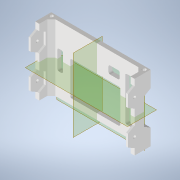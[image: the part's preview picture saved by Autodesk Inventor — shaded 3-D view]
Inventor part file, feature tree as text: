
AUTODESK INVENTOR PART (.ipt)
format: ipt  version: 2022.2 (Build 262287000, 287)  size: 368,128 bytes
history: native  units: mm
features: reference x24, extrude x12, sketch x12, projected_geometry x6, other x6, plane x3, chamfer x2, mirror x2, shell x1, fillet x1
ambient origin geometry x8: Origin, YZ Plane, XZ Plane, XY Plane, X Axis, Y Axis, Z Axis, Center Point
bodies: Solid1 (feature_tree)
feature tree (69):
  plane  "Work Plane1"
  extrude  "Extrusion1"  Depth=20.0mm
  extrude  "Extrusion2"  Depth=8.0mm TaperAngle=45.0deg
  chamfer  "Chamfer1"  Distance=25.0mm
  shell  "Shell1"  Thickness=150.0deg
  extrude  "Extrusion5"  Depth=20.0mm
  extrude  "Extrusion6"  TaperAngle=60.0deg  [1 undecoded]
  extrude  "Extrusion8"  Depth=8.0mm
  extrude  "Extrusion10"  Depth=8.0mm
  extrude  "Extrusion11"  Depth=8.0mm
  extrude  "Extrusion7"  Depth=10.0mm
  plane  "Work Plane3"
  plane  "Work Plane4"
  mirror  "Mirror2"
  mirror  "Mirror3"
  chamfer  "Chamfer4"  [1 undecoded]
  extrude  "Extrusion14"  TaperAngle=60.0deg  [1 undecoded]
  extrude  "Extrusion15"  TaperAngle=60.0deg  [1 undecoded]
  extrude  "Extrusion16"  Depth=8.0mm
  extrude  "Extrusion17"  Depth=62.5mm
  fillet  "Fillet6"  Radius=42.5mm
  sketch  "Sketch3"  dims[d1=20.0mm d2=0.0mm d3=4.0mm]
  reference  "Reference1"
  reference  "Reference2"
  reference  "Reference3"
  reference  "Reference4"
  reference  "Reference5"
  reference  "Reference6"
  reference  "Reference7"
  reference  "Reference8"
  reference  "Reference9"
  reference  "Reference10"
  reference  "Reference11"
  reference  "Reference12"
  sketch  "Sketch4"  dims[d4=0.0mm d5=0.0mm d6=8.0mm d7=2.0mm d8=45.0deg]
  reference  "Reference13"
  sketch  "Sketch7"  dims[d9=5.0mm d27=25.0mm d28=0.0mm d29=150.0deg]
  projected_geometry  "Projected Loop2"
  sketch  "Sketch8"  dims[d30=20.0mm d31=0.0mm d37=3.5mm]
  projected_geometry  "Projected Loop3"
  sketch  "Sketch10"  dims[d38=12.0mm d39=0.436332mm d43=60.0deg]
  projected_geometry  "Projected Loop5"
  sketch  "Sketch12"  dims[d44=60.0deg d45=8.0mm]
  projected_geometry  "Projected Loop7"
  sketch  "Sketch15"  dims[d46=15.0mm d47=8.0mm]
  projected_geometry  "Projected Loop9"
  sketch  "Sketch16"  dims[d48=2.5mm d49=0.0mm d53=8.0mm]
  projected_geometry  "Projected Loop10"
  sketch  "Sketch19"  dims[d59=10.0mm d60=0.0mm d61=3.5mm d62=0.0mm d63=0.0mm]
  reference  "Reference14"
  reference  "Reference15"
  reference  "Reference16"
  reference  "Reference17"
  sketch  "Sketch20"  dims[d67=0.5mm d68=2.0mm d69=45.0deg d79=60.0deg]
  reference  "Reference18"
  reference  "Reference19"
  reference  "Reference20"
  reference  "Reference21"
  sketch  "Sketch21"  dims[d80=60.0deg d81=60.0deg]
  reference  "Reference22"
  reference  "Reference23"
  sketch  "Sketch22"  dims[d82=60.0deg d84=8.0mm d85=62.5mm d86=42.5mm d87=0.0mm d88=0.0mm d90=8.0mm d91=8.0mm d92=12.0mm d93=12.0mm d94=2.0mm d95=0.0mm d96=0.0mm d98=2.0mm d99=0.0mm d100=0.0mm d102=2.0mm d103=0.0mm d104=0.0mm d105=2.0mm]
  reference  "Reference25"
  other  "<userpath>\Desktop\Jetson-Nano-2GB-Case\A.iam"
  other  "A.iam"
  other  "A-00:1"
  other  "Jetson Nano 2GB:1"
  other  "642-13541_BATUU_SYS_BOM_ASM:1"
  other  "600-13542-BASE-A02_ASM:1"
note: 4 required parameter values undecoded (feature->parameter linkage not recoverable at this tier; creation-order binding heuristic only, values carry confidence <= 0.55)
